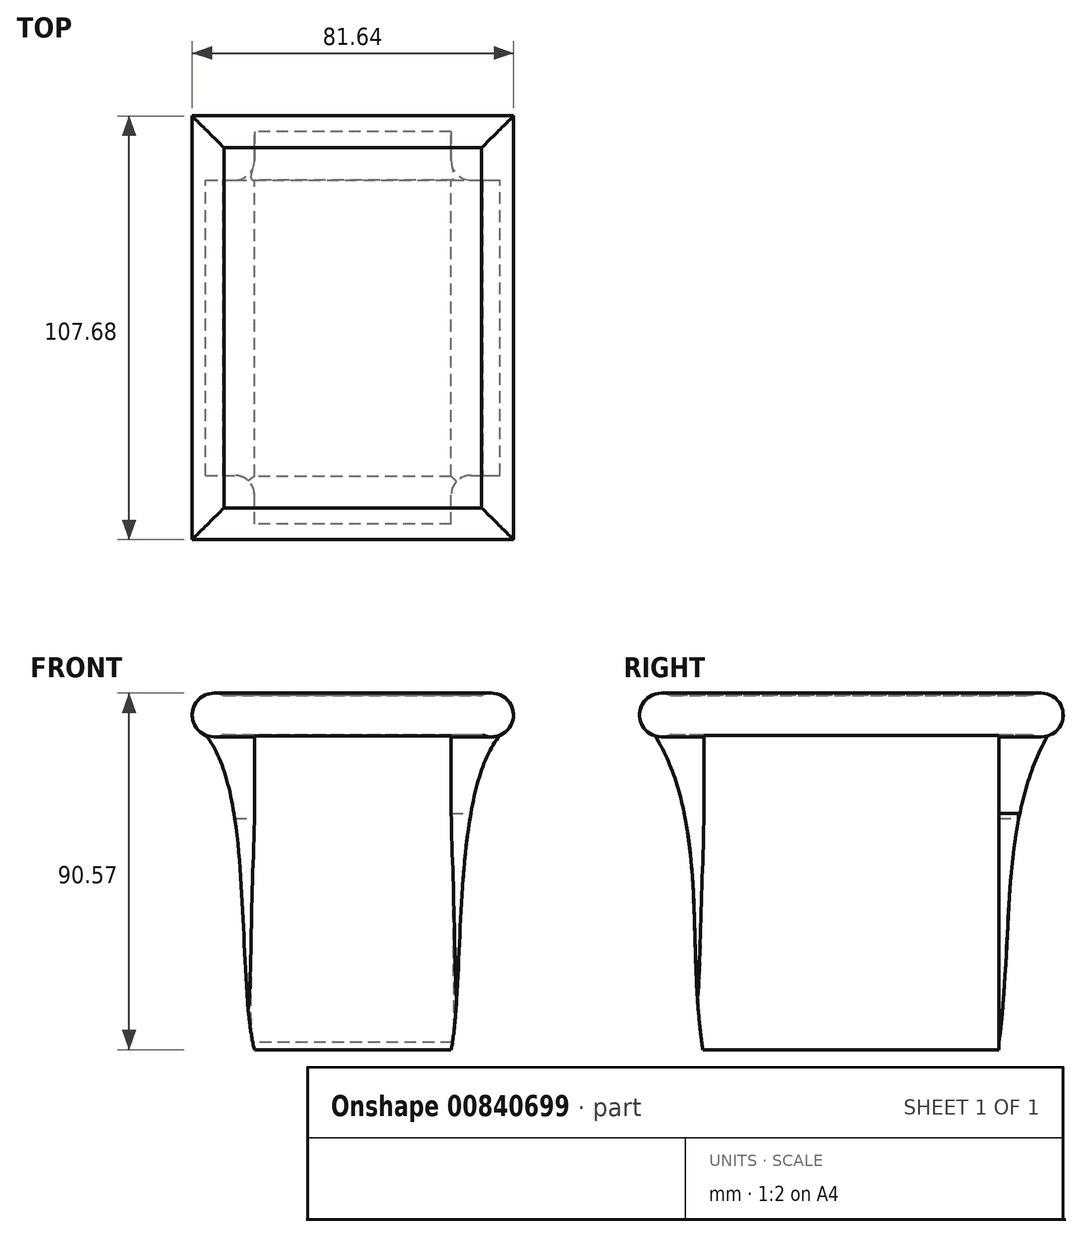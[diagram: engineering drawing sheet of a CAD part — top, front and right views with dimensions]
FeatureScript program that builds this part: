
annotation { "Feature Type Name" : "Feature", "Feature Type Description" : "" }
export const myFeature = defineFeature(function(context is Context, id is Id, definition is map)
    precondition{}
    {
        {
            var Q0;
            Q0=qCreatedBy(makeId("Front.planeOp"),FACE);
            var sketch = newSketch(context, id + "F0", { "sketchPlane" : qUnion([Q0])});
            skLineSegment(sketch, "E0.bottom", {"start": v(-25, 0) * mm, "end": v(25, 0) * mm});
            skLineSegment(sketch, "E0.top", {"start": v(-25, 80) * mm, "end": v(25, 80) * mm});
            skLineSegment(sketch, "E1", {"start": v(-37.5, 80) * mm, "end": v(37.5, 80) * mm});
            skFitSpline(sketch, "E2", {"points": [v(-37.5, 80) * mm, v(-25, 0) * mm], "startDerivative": vector(37.5, -43.44) * mm, "endDerivative": vector(13.99, -54.98) * mm});
            skFitSpline(sketch, "E3", {"points": [v(25, 0) * mm, v(37.5, 80) * mm], "startDerivative": vector(10.53, 54.98) * mm, "endDerivative": vector(37.5, 43.44) * mm});
            skSolve(sketch);
        }
        {
            var Q0;
            Q0 = qSketchRegion(id + "F0", true);
            extrude(context, id + "F1", {"entities" : qUnion([Q0]), "depth" : 37.5 * mm, "offsetDistance" : 25 * mm, "hasSecondDirection" : true, "secondDirectionOppositeDirection" : true, "secondDirectionDepth" : 37.5 * mm});
        }
        {
            var Q0;
            Q0=qCreatedBy(makeId("Right.planeOp"),FACE);
            var sketch = newSketch(context, id + "F2", { "sketchPlane" : qUnion([Q0])});
            skLineSegment(sketch, "E4", {"start": v(-50, 80) * mm, "end": v(50, 80) * mm});
            skFitSpline(sketch, "E5", {"points": [v(-50, 80) * mm, v(-37.75, 0) * mm], "startDerivative": vector(41.46, -67.14) * mm, "endDerivative": vector(12.51, -80.09) * mm});
            skFitSpline(sketch, "E6", {"points": [v(50, 80) * mm, v(37.23, 0) * mm], "startDerivative": vector(-38.32, -67.14) * mm, "endDerivative": vector(-12.25, -80.09) * mm});
            skLineSegment(sketch, "E7", {"start": v(-37.75, 0) * mm, "end": v(37.23, 0) * mm});
            skSolve(sketch);
        }
        {
            var Q0;
            Q0 = qSketchRegion(id + "F2", true);
            extrude(context, id + "F3", {"entities" : qUnion([Q0]), "operationType" : NewBodyOperationType.ADD, "depth" : 25 * mm, "offsetDistance" : 25 * mm, "hasSecondDirection" : true, "secondDirectionOppositeDirection" : true, "secondDirectionDepth" : 25 * mm});
        }
        {
            var Q0;
            Q0=makeQuery(id+"F3.boolean.opBoolean","INTERSECT",EDGE,{"derivedFrom":[makeQuery(id+"F1.opExtrude","CAP_FACE",FACE,{"disambiguationData":[OSD([sQuery(id+"F0.wireOp",EDGE,"E0.bottom"),sQuery(id+"F0.wireOp",EDGE,"E1"),sQuery(id+"F0.wireOp",EDGE,"E2"),sQuery(id+"F0.wireOp",EDGE,"E3")])],"isStart":false}),makeQuery(id+"F3.opExtrude","CAP_FACE",FACE,{"disambiguationData":[OSD([sQuery(id+"F2.wireOp",EDGE,"E4"),sQuery(id+"F2.wireOp",EDGE,"E5"),sQuery(id+"F2.wireOp",EDGE,"E6"),sQuery(id+"F2.wireOp",EDGE,"E7")])],"isStart":true})]});
            var Q1;
            Q1=makeQuery(id+"F3.boolean.opBoolean","INTERSECT",EDGE,{"derivedFrom":[makeQuery(id+"F1.opExtrude","CAP_FACE",FACE,{"disambiguationData":[OSD([sQuery(id+"F0.wireOp",EDGE,"E0.bottom"),sQuery(id+"F0.wireOp",EDGE,"E1"),sQuery(id+"F0.wireOp",EDGE,"E2"),sQuery(id+"F0.wireOp",EDGE,"E3")])],"isStart":false}),makeQuery(id+"F3.opExtrude","CAP_FACE",FACE,{"disambiguationData":[OSD([sQuery(id+"F2.wireOp",EDGE,"E4"),sQuery(id+"F2.wireOp",EDGE,"E5"),sQuery(id+"F2.wireOp",EDGE,"E6"),sQuery(id+"F2.wireOp",EDGE,"E7")])],"isStart":false})]});
            var Q2;
            Q2=makeQuery(id+"F3.boolean.opBoolean","INTERSECT",EDGE,{"derivedFrom":[makeQuery(id+"F1.opExtrude","CAP_FACE",FACE,{"disambiguationData":[OSD([sQuery(id+"F0.wireOp",EDGE,"E0.bottom"),sQuery(id+"F0.wireOp",EDGE,"E1"),sQuery(id+"F0.wireOp",EDGE,"E2"),sQuery(id+"F0.wireOp",EDGE,"E3")])],"isStart":true}),makeQuery(id+"F3.opExtrude","CAP_FACE",FACE,{"disambiguationData":[OSD([sQuery(id+"F2.wireOp",EDGE,"E4"),sQuery(id+"F2.wireOp",EDGE,"E5"),sQuery(id+"F2.wireOp",EDGE,"E6"),sQuery(id+"F2.wireOp",EDGE,"E7")])],"isStart":false})]});
            var Q3;
            Q3=makeQuery(id+"F3.boolean.opBoolean","INTERSECT",EDGE,{"derivedFrom":[makeQuery(id+"F1.opExtrude","CAP_FACE",FACE,{"disambiguationData":[OSD([sQuery(id+"F0.wireOp",EDGE,"E0.bottom"),sQuery(id+"F0.wireOp",EDGE,"E1"),sQuery(id+"F0.wireOp",EDGE,"E2"),sQuery(id+"F0.wireOp",EDGE,"E3")])],"isStart":true}),makeQuery(id+"F3.opExtrude","CAP_FACE",FACE,{"disambiguationData":[OSD([sQuery(id+"F2.wireOp",EDGE,"E4"),sQuery(id+"F2.wireOp",EDGE,"E5"),sQuery(id+"F2.wireOp",EDGE,"E6"),sQuery(id+"F2.wireOp",EDGE,"E7")])],"isStart":true})]});
            fillet(context, id + "F4", {"entities" : qUnion([Q0, Q1, Q2, Q3]), "radius" : 5 * mm, "tangentPropagation" : true, "allowEdgeOverflow" : false});
        }
        {
            var Q0;
            Q0=makeQuery(id+"F3.boolean.opBoolean","MERGE",FACE,{"derivedFrom":[makeQuery(id+"F1.opExtrude","SWEPT_FACE",FACE,{"disambiguationData":[OSD([sQuery(id+"F0.wireOp",EDGE,"E1")])]}),makeQuery(id+"F3.opExtrude","SWEPT_FACE",FACE,{"disambiguationData":[OSD([sQuery(id+"F2.wireOp",EDGE,"E4")])]})]});
            var sketch = newSketch(context, id + "F5", { "sketchPlane" : qUnion([Q0])});
            skLineSegment(sketch, "E8.bottom", {"start": v(32.74, 45.76) * mm, "end": v(-32.74, 45.76) * mm});
            skLineSegment(sketch, "E8.top", {"start": v(32.74, -45.76) * mm, "end": v(-32.74, -45.76) * mm});
            skLineSegment(sketch, "E8.left", {"start": v(32.74, 45.76) * mm, "end": v(32.74, -45.76) * mm});
            skLineSegment(sketch, "E8.right", {"start": v(-32.74, 45.76) * mm, "end": v(-32.74, -45.76) * mm});
            skPoint(sketch, "E8.middle", {"position": v(0, 0) * mm});
            skSolve(sketch);
        }
        {
            var Q0;
            Q0 = qSketchRegion(id + "F5", true);
            extrude(context, id + "F6", {"entities" : qUnion([Q0]), "operationType" : NewBodyOperationType.ADD, "depth" : 10 * mm, "offsetDistance" : 25 * mm});
        }
        {
            var Q0;
            Q0=qCreatedBy(makeId("Top.planeOp"),FACE);
            cPlane(context, id + "F7", {"entities" : qUnion([Q0]), "cplaneType" : CPlaneType.OFFSET, "offset" : 85 * mm, "width" : 150 * mm, "height" : 150 * mm});
        }
        {
            var Q0;
            Q0=qCreatedBy(makeId("Front.planeOp"),FACE);
            var sketch = newSketch(context, id + "F8", { "sketchPlane" : qUnion([Q0])});
            skCircle(sketch, "E9", {"center": v(35.27, 85.02) * mm, "radius": 5.55 * mm});
            skSolve(sketch);
        }
        {
            var Q0;
            Q0=makeQuery(id+"F8.imprint","IMPRINT",FACE,{"disambiguationData":[TD([[makeQuery(id+"F8.imprint","IMPRINT",EDGE,{"derivedFrom":sQuery(id+"F8.wireOp",EDGE,"E9")}),1.0]])]});
            var Q1;
            Q1=makeQuery(id+"F6.opExtrude","CAP_EDGE",EDGE,{"disambiguationData":[OSD([sQuery(id+"F5.wireOp",EDGE,"E8.left")])],"isStart":false});
            var Q2;
            Q2=makeQuery(id+"F6.opExtrude","CAP_EDGE",EDGE,{"disambiguationData":[OSD([sQuery(id+"F5.wireOp",EDGE,"E8.bottom")])],"isStart":false});
            var Q3;
            Q3=makeQuery(id+"F6.opExtrude","CAP_EDGE",EDGE,{"disambiguationData":[OSD([sQuery(id+"F5.wireOp",EDGE,"E8.right")])],"isStart":false});
            var Q4;
            Q4=makeQuery(id+"F6.opExtrude","CAP_EDGE",EDGE,{"disambiguationData":[OSD([sQuery(id+"F5.wireOp",EDGE,"E8.top")])],"isStart":false});
            sweep(context, id + "F9", {"operationType" : NewBodyOperationType.ADD, "profiles" : qUnion([Q0]), "path" : qUnion([Q1, Q2, Q3, Q4])});
        }
    });
